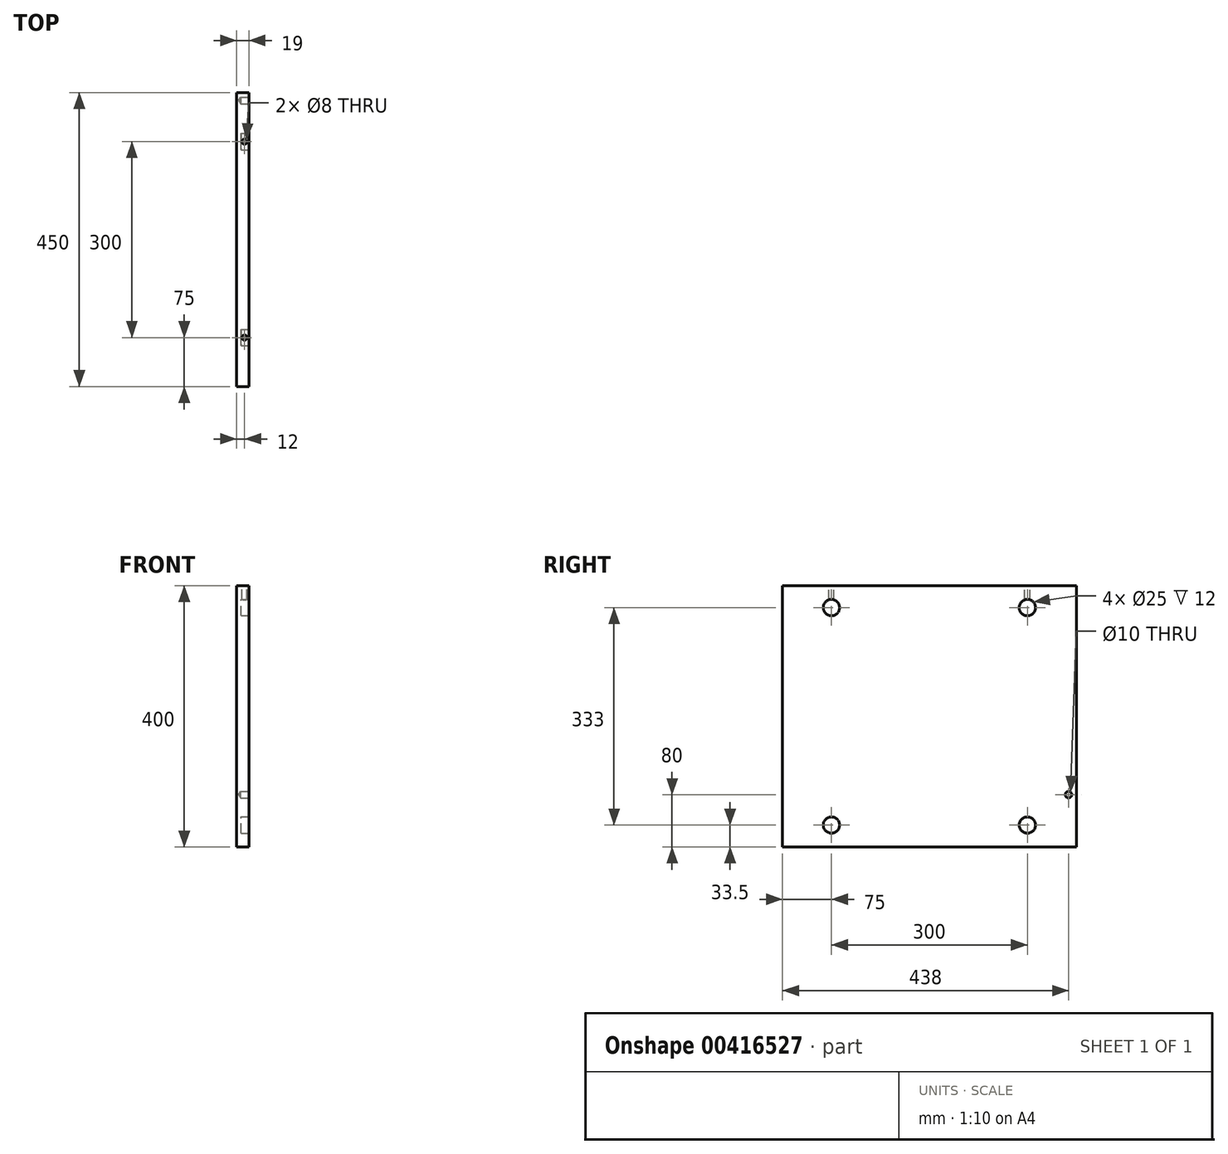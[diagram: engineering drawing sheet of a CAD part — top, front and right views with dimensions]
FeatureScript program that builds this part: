
annotation { "Feature Type Name" : "Feature", "Feature Type Description" : "" }
export const myFeature = defineFeature(function(context is Context, id is Id, definition is map)
    precondition{}
    {
        {
            var Q0;
            Q0=qCreatedBy(makeId("Right.planeOp"),FACE);
            var sketch = newSketch(context, id + "F0", { "sketchPlane" : qUnion([Q0])});
            skLineSegment(sketch, "E0.bottom", {"start": v(225, 200) * mm, "end": v(-225, 200) * mm});
            skLineSegment(sketch, "E0.top", {"start": v(225, -200) * mm, "end": v(-225, -200) * mm});
            skLineSegment(sketch, "E0.left", {"start": v(225, 200) * mm, "end": v(225, -200) * mm});
            skLineSegment(sketch, "E0.right", {"start": v(-225, 200) * mm, "end": v(-225, -200) * mm});
            skPoint(sketch, "E0.middle", {"position": v(0, 0) * mm});
            skSolve(sketch);
        }
        {
            var Q0;
            Q0=makeQuery(id+"F0.imprint","IMPRINT",FACE,{"disambiguationData":[TD([[makeQuery(id+"F0.imprint","IMPRINT",EDGE,{"derivedFrom":sQuery(id+"F0.wireOp",EDGE,"E0.bottom")}),1.0]])]});
            extrude(context, id + "F1", {"entities" : qUnion([Q0]), "oppositeDirection" : true, "depth" : 19 * mm});
        }
        {
            var Q0;
            Q0=makeQuery(id+"F1.opExtrude","CAP_FACE",FACE,{"disambiguationData":[OSD([sQuery(id+"F0.wireOp",EDGE,"E0.bottom"),sQuery(id+"F0.wireOp",EDGE,"E0.top"),sQuery(id+"F0.wireOp",EDGE,"E0.left"),sQuery(id+"F0.wireOp",EDGE,"E0.right")])],"isStart":true});
            var sketch = newSketch(context, id + "F2", { "sketchPlane" : qUnion([Q0])});
            skLineSegment(sketch, "E1", {"start": v(-150, 279.69) * mm, "end": v(-150, -246.57) * mm, "construction": true});
            skLineSegment(sketch, "E2", {"start": v(150, 275.12) * mm, "end": v(150, -261.19) * mm, "construction": true});
            skLineSegment(sketch, "E3", {"start": v(-280.73, 166.5) * mm, "end": v(270.25, 166.5) * mm, "construction": true});
            skLineSegment(sketch, "E4", {"start": v(-283.5, -166.5) * mm, "end": v(272.11, -166.5) * mm, "construction": true});
            skCircle(sketch, "E5", {"center": v(-150, 166.5) * mm, "radius": 12.5 * mm});
            skCircle(sketch, "E6", {"center": v(150, 166.5) * mm, "radius": 12.5 * mm});
            skCircle(sketch, "E7", {"center": v(-150, -166.5) * mm, "radius": 12.5 * mm});
            skCircle(sketch, "E8", {"center": v(150, -166.5) * mm, "radius": 12.5 * mm});
            skSolve(sketch);
        }
        {
            var Q0;
            Q0=makeQuery(id+"F2.imprint","IMPRINT",FACE,{"disambiguationData":[TD([[makeQuery(id+"F2.imprint","IMPRINT",EDGE,{"derivedFrom":sQuery(id+"F2.wireOp",EDGE,"E7")}),1.0]])]});
            var Q1;
            Q1=makeQuery(id+"F2.imprint","IMPRINT",FACE,{"disambiguationData":[TD([[makeQuery(id+"F2.imprint","IMPRINT",EDGE,{"derivedFrom":sQuery(id+"F2.wireOp",EDGE,"E8")}),1.0]])]});
            var Q2;
            Q2=makeQuery(id+"F2.imprint","IMPRINT",FACE,{"disambiguationData":[TD([[makeQuery(id+"F2.imprint","IMPRINT",EDGE,{"derivedFrom":sQuery(id+"F2.wireOp",EDGE,"E5")}),1.0]])]});
            var Q3;
            Q3=makeQuery(id+"F2.imprint","IMPRINT",FACE,{"disambiguationData":[TD([[makeQuery(id+"F2.imprint","IMPRINT",EDGE,{"derivedFrom":sQuery(id+"F2.wireOp",EDGE,"E6")}),1.0]])]});
            extrude(context, id + "F3", {"entities" : qUnion([Q0, Q1, Q2, Q3]), "operationType" : NewBodyOperationType.REMOVE, "oppositeDirection" : true, "depth" : 12 * mm});
        }
        {
            var Q0;
            {var subQ0=sQuery(id+"F0.wireOp",EDGE,"E0.bottom");Q0=makeQuery(id+"F3.boolean.opBoolean","MERGE",FACE,{"derivedFrom":[makeQuery(id+"F1.opExtrude","SWEPT_FACE",FACE,{"disambiguationData":[OSD([subQ0])]}),makeQuery(id+"F3.opExtrude","SWEPT_FACE",FACE,{"disambiguationData":[OSD([subQ0])]})]});}
            var sketch = newSketch(context, id + "F4", { "sketchPlane" : qUnion([Q0])});
            skLineSegment(sketch, "E9", {"start": v(37.22, 150) * mm, "end": v(-42.68, 150) * mm, "construction": true});
            skLineSegment(sketch, "E10", {"start": v(27.4, -150) * mm, "end": v(-41.4, -150) * mm, "construction": true});
            skPoint(sketch, "E11", {"position": v(-7, -150) * mm});
            skPoint(sketch, "E12", {"position": v(-7, 150) * mm});
            skSolve(sketch);
        }
        {
            var Q0;
            Q0=sQuery(id+"F4.wireOp",VERTEX,"E12");
            var Q1;
            Q1=sQuery(id+"F4.wireOp",VERTEX,"E11");
            var Q2;
            Q2=makeQuery(id+"F1.opExtrude","SWEPT_BODY",BODY,{"disambiguationData":[OSD([sQuery(id+"F0.wireOp",EDGE,"E0.bottom"),sQuery(id+"F0.wireOp",EDGE,"E0.top"),sQuery(id+"F0.wireOp",EDGE,"E0.left"),sQuery(id+"F0.wireOp",EDGE,"E0.right")])]});
            hole(context, id + "F5", {"style" : HoleStyle.SIMPLE, "endStyle" : HoleEndStyle.BLIND, "holeDiameter" : 8 * mm, "holeDepth" : 22 * mm, "isTappedThrough" : true, "tappedDepth" : 12 * mm, "tapClearance" : 3, "startFromSketch" : true, "locations" : qUnion([Q0, Q1]), "scope" : qUnion([Q2])});
        }
        {
            var Q0;
            Q0=makeQuery(id+"F1.opExtrude","CAP_FACE",FACE,{"disambiguationData":[OSD([sQuery(id+"F0.wireOp",EDGE,"E0.bottom"),sQuery(id+"F0.wireOp",EDGE,"E0.top"),sQuery(id+"F0.wireOp",EDGE,"E0.left"),sQuery(id+"F0.wireOp",EDGE,"E0.right")])],"isStart":true});
            var sketch = newSketch(context, id + "F6", { "sketchPlane" : qUnion([Q0])});
            skPoint(sketch, "E13", {"position": v(213, -120) * mm});
            skSolve(sketch);
        }
        {
            var Q0;
            Q0=sQuery(id+"F6.wireOp",VERTEX,"E13");
            var Q1;
            Q1=makeQuery(id+"F1.opExtrude","SWEPT_BODY",BODY,{"disambiguationData":[OSD([sQuery(id+"F0.wireOp",EDGE,"E0.bottom"),sQuery(id+"F0.wireOp",EDGE,"E0.top"),sQuery(id+"F0.wireOp",EDGE,"E0.left"),sQuery(id+"F0.wireOp",EDGE,"E0.right")])]});
            hole(context, id + "F7", {"style" : HoleStyle.SIMPLE, "endStyle" : HoleEndStyle.BLIND, "holeDiameter" : 10 * mm, "holeDepth" : 13 * mm, "isTappedThrough" : true, "tappedDepth" : 12 * mm, "tapClearance" : 3, "startFromSketch" : true, "locations" : qUnion([Q0]), "scope" : qUnion([Q1])});
        }
    });
